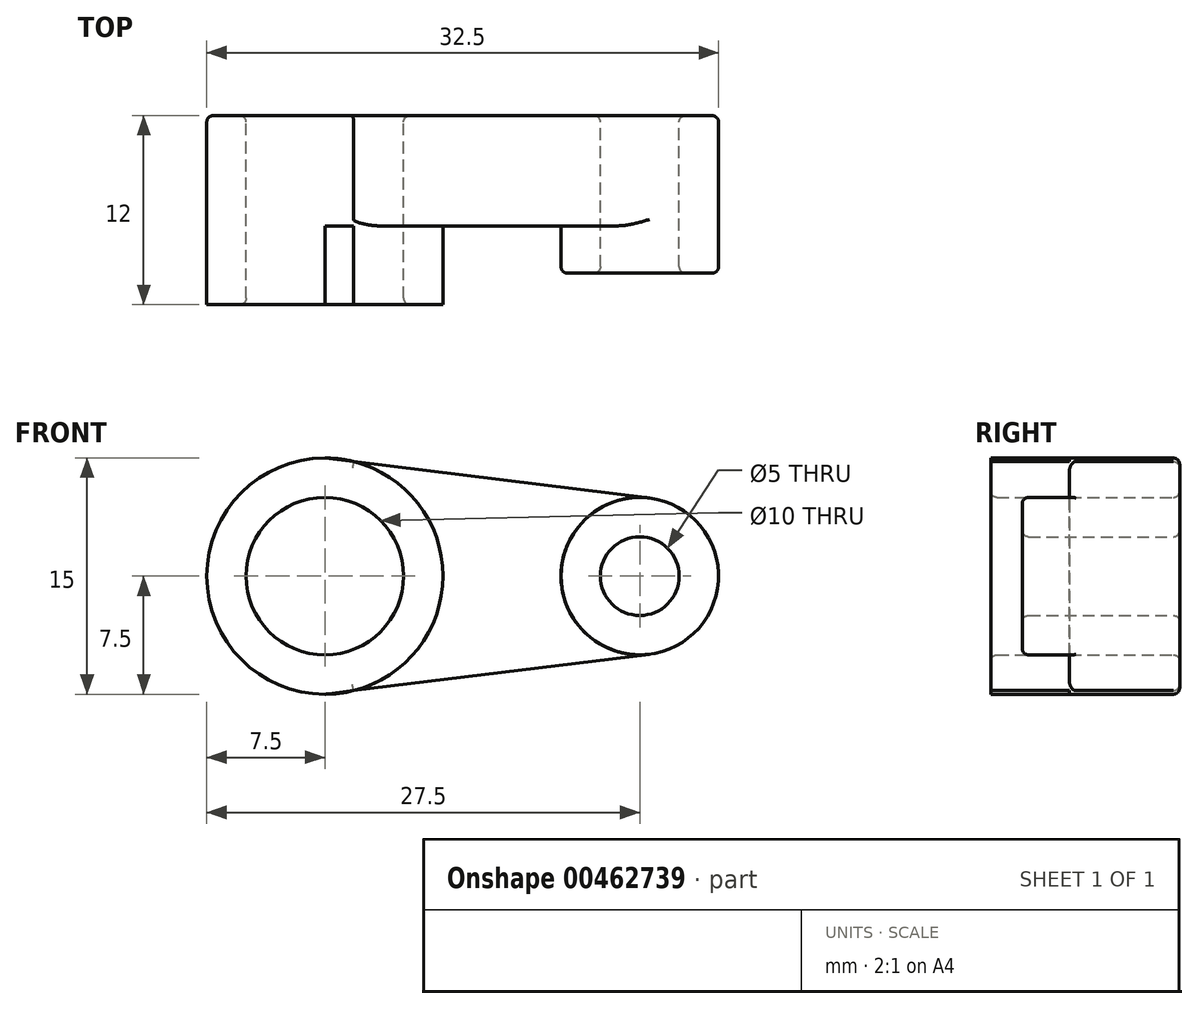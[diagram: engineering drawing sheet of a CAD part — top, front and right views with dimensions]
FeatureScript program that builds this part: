
annotation { "Feature Type Name" : "Feature", "Feature Type Description" : "" }
export const myFeature = defineFeature(function(context is Context, id is Id, definition is map)
    precondition{}
    {
        {
            var Q0;
            Q0=qCreatedBy(makeId("Front.planeOp"),FACE);
            var sketch = newSketch(context, id + "F0", { "sketchPlane" : qUnion([Q0])});
            skCircle(sketch, "E0", {"center": v(0, 0) * mm, "radius": 7.5 * mm});
            skCircle(sketch, "E1", {"center": v(20, 0) * mm, "radius": 5 * mm});
            skLineSegment(sketch, "E2", {"start": v(0, 7.5) * mm, "end": v(20.61, 4.96) * mm});
            skLineSegment(sketch, "E3", {"start": v(0, -7.5) * mm, "end": v(20.61, -4.96) * mm});
            skCircle(sketch, "E4", {"center": v(0, 0) * mm, "radius": 5 * mm});
            skCircle(sketch, "E5", {"center": v(20, 0) * mm, "radius": 2.5 * mm});
            skSolve(sketch);
        }
        {
            var Q0;
            Q0 = qSketchRegion(id + "F0", true);
            extrude(context, id + "F1", {"entities" : qUnion([Q0]), "depth" : 7 * mm});
        }
        {
            var Q0;
            Q0=makeQuery(id+"F0.imprint","IMPRINT",FACE,{"disambiguationData":[TD([[makeQuery(id+"F0.imprint","IMPRINT",EDGE,{"derivedFrom":sQuery(id+"F0.wireOp",EDGE,"E5")}),-1.0]])]});
            extrude(context, id + "F2", {"entities" : qUnion([Q0]), "operationType" : NewBodyOperationType.ADD, "depth" : 10 * mm});
        }
        {
            var Q0;
            Q0=makeQuery(id+"F0.imprint","IMPRINT",FACE,{"disambiguationData":[TD([[makeQuery(id+"F0.imprint","IMPRINT",EDGE,{"derivedFrom":sQuery(id+"F0.wireOp",EDGE,"E4")}),-1.0]])]});
            extrude(context, id + "F3", {"entities" : qUnion([Q0]), "operationType" : NewBodyOperationType.ADD, "depth" : 12 * mm});
        }
        {
            var Q0;
            {var subQ0=sQuery(id+"F0.wireOp",EDGE,"E0");Q0=makeQuery(id+"F3.opExtrude","CAP_EDGE",EDGE,{"disambiguationData":[OSD([subQ0]),TDD([makeQuery(id+"F0.imprint","IMPRINT",EDGE,{"disambiguationData":[TD([[makeQuery(id+"F0.imprint","INTERSECT",VERTEX,{"disambiguationData":[OD(0.0)],"derivedFrom":[subQ0,sQuery(id+"F0.wireOp",EDGE,"E2")]}),-1.0]])],"derivedFrom":subQ0})])],"isStart":false});}
            var Q1;
            Q1=makeQuery(id+"F3.opExtrude","CAP_EDGE",EDGE,{"disambiguationData":[OSD([sQuery(id+"F0.wireOp",EDGE,"E4")])],"isStart":false});
            var Q2;
            Q2=makeQuery(id+"F2.opExtrude","CAP_EDGE",EDGE,{"disambiguationData":[OSD([sQuery(id+"F0.wireOp",EDGE,"E5")])],"isStart":false});
            var Q3;
            Q3=makeQuery(id+"F2.opExtrude","CAP_EDGE",EDGE,{"disambiguationData":[OSD([sQuery(id+"F0.wireOp",EDGE,"E1")])],"isStart":false});
            var Q4;
            {var subQ0=sQuery(id+"F0.wireOp",EDGE,"E0");Q4=makeQuery(id+"F3.opExtrude","CAP_EDGE",EDGE,{"disambiguationData":[OSD([subQ0]),TDD([makeQuery(id+"F0.imprint","IMPRINT",EDGE,{"disambiguationData":[TD([[makeQuery(id+"F0.imprint","INTERSECT",VERTEX,{"disambiguationData":[OD(1.0)],"derivedFrom":[subQ0,sQuery(id+"F0.wireOp",EDGE,"E2")]}),1.0]])],"derivedFrom":subQ0})])],"isStart":false});}
            var Q5;
            Q5=makeQuery(id+"F1.opExtrude","CAP_EDGE",EDGE,{"disambiguationData":[OSD([sQuery(id+"F0.wireOp",EDGE,"E0")])],"isStart":true});
            var Q6;
            Q6=makeQuery(id+"F1.opExtrude","CAP_EDGE",EDGE,{"disambiguationData":[OSD([sQuery(id+"F0.wireOp",EDGE,"E4")])],"isStart":true});
            var Q7;
            Q7=makeQuery(id+"F1.opExtrude","CAP_EDGE",EDGE,{"disambiguationData":[OSD([sQuery(id+"F0.wireOp",EDGE,"E5")])],"isStart":true});
            var Q8;
            Q8=makeQuery(id+"F1.opExtrude","CAP_EDGE",EDGE,{"disambiguationData":[OSD([sQuery(id+"F0.wireOp",EDGE,"E1")])],"isStart":true});
            var Q9;
            Q9=makeQuery(id+"F1.opExtrude","CAP_EDGE",EDGE,{"disambiguationData":[OSD([sQuery(id+"F0.wireOp",EDGE,"E2")])],"isStart":true});
            var Q10;
            Q10=makeQuery(id+"F1.opExtrude","CAP_FACE",FACE,{"disambiguationData":[OSD([sQuery(id+"F0.wireOp",EDGE,"E0"),sQuery(id+"F0.wireOp",EDGE,"E1"),sQuery(id+"F0.wireOp",EDGE,"E2"),sQuery(id+"F0.wireOp",EDGE,"E3"),sQuery(id+"F0.wireOp",EDGE,"E4"),sQuery(id+"F0.wireOp",EDGE,"E5")])],"isStart":true});
            var Q11;
            Q11=makeQuery(id+"F1.opExtrude","CAP_EDGE",EDGE,{"disambiguationData":[OSD([sQuery(id+"F0.wireOp",EDGE,"E2")])],"isStart":false});
            var Q12;
            Q12=makeQuery(id+"F1.opExtrude","CAP_EDGE",EDGE,{"disambiguationData":[OSD([sQuery(id+"F0.wireOp",EDGE,"E3")])],"isStart":false});
            fillet(context, id + "F4", {"entities" : qUnion([Q0, Q1, Q2, Q3, Q4, Q5, Q6, Q7, Q8, Q9, Q10, Q11, Q12]), "radius" : 0.4 * mm, "tangentPropagation" : true, "allowEdgeOverflow" : false});
        }
    });
